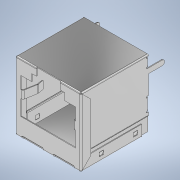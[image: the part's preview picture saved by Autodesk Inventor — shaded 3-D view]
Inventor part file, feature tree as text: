
AUTODESK INVENTOR PART (.ipt)
format: ipt  version: 2020.1 (Build 241239000, 239)  size: 926,208 bytes
history: native  units: mm
features: sheet_metal_op x45, sketch x21, other x20, mirror x7, fillet x1, chamfer x1
ambient origin geometry x8: Origin, YZ Plane, XZ Plane, XY Plane, X Axis, Y Axis, Z Axis, Center Point
bodies: Solid1 (feature_tree)
feature tree (95):
  sheet_metal_op  "Face1"
  sheet_metal_op  "Flange1"
  sheet_metal_op  "Flange2"
  other  "Corner Chamfer1"
  mirror  "Mirror1"
  sheet_metal_op  "Face2"
  mirror  "Mirror2"
  sheet_metal_op  "Fold2"
  mirror  "Mirror3"
  sheet_metal_op  "Fold3"
  sheet_metal_op  "Fold5"
  mirror  "Mirror4"
  sheet_metal_op  "Flange5"
  sketch  "Sketch15"  dims[d11=0.2mm]
  sheet_metal_op  "Face3"
  sheet_metal_op  "Fold7"
  mirror  "Mirror6"
  sheet_metal_op  "Flange8"
  sheet_metal_op  "Flange9"
  sheet_metal_op  "Flange10"
  sheet_metal_op  "Flange11"
  sheet_metal_op  "Flange12"
  sheet_metal_op  "Flange13"
  sheet_metal_op  "Flange14"
  fillet  "Fillet1"  Radius=15.3mm
  mirror  "Mirror7"
  sheet_metal_op  "Flange15"
  sheet_metal_op  "Flange16"
  chamfer  "Corner Round1"
  mirror  "Mirror9"
  sketch  "Sketch1"  dims[d1=16.05mm]
  other  "Plate1"
  sketch  "Sketch3"  dims[d2=0.2mm]
  other  "Plate2"
  sheet_metal_op  "Bend1"
  sheet_metal_op  "Corner1"
  sketch  "Sketch4"  dims[d3=0.435mm]
  other  "Plate3"
  sheet_metal_op  "Bend2"
  sheet_metal_op  "Corner2"
  sketch  "Sketch9"  dims[d4=0.2175mm]
  other  "Plate6"
  sheet_metal_op  "Bend5"
  sketch  "Sketch11"  dims[d5=0.0mm]
  sketch  "Sketch12"  dims[d6=0.1mm]
  sketch  "Sketch13"  dims[d7=16.4mm d8=90.0deg d9=0.1mm]
  sketch  "Sketch14"  dims[d10=0.8mm]
  other  "Plate7"
  sheet_metal_op  "Bend6"
  sheet_metal_op  "Corner5"
  other  "Plate8"
  sheet_metal_op  "Bend7"
  sketch  "Sketch20"  dims[d12=0.1mm]
  sketch  "Sketch21"  dims[d13=0.435mm]
  other  "Plate11"
  sheet_metal_op  "Bend10"
  sheet_metal_op  "Corner8"
  sketch  "Sketch22"  dims[d14=0.2175mm]
  other  "Plate12"
  sheet_metal_op  "Bend11"
  sheet_metal_op  "Corner9"
  sketch  "Sketch23"  dims[d15=0.0mm]
  other  "Plate13"
  sheet_metal_op  "Bend12"
  sheet_metal_op  "Corner10"
  sketch  "Sketch24"  dims[d16=0.1mm]
  other  "Plate14"
  sheet_metal_op  "Bend13"
  sheet_metal_op  "Corner11"
  sketch  "Sketch25"  dims[d17=2.2mm d18=90.0deg d19=0.1mm]
  other  "Plate15"
  sheet_metal_op  "Bend14"
  sheet_metal_op  "Corner12"
  sketch  "Sketch26"  dims[d20=0.8mm]
  other  "Plate16"
  sheet_metal_op  "Bend15"
  sheet_metal_op  "Corner13"
  sketch  "Sketch27"  dims[d21=0.2mm]
  other  "Plate17"
  sheet_metal_op  "Bend16"
  sheet_metal_op  "Corner14"
  sketch  "Sketch28"  dims[d22=0.1mm]
  sketch  "Sketch29"  dims[d23=2.1mm d24=6.0mm d25=45.0deg]
  sketch  "Sketch30"  dims[d51=45.0deg]
  other  "Plate18"
  sheet_metal_op  "Bend17"
  sheet_metal_op  "Corner15"
  sketch  "Sketch31"  dims[d54=16.4mm d55=0.1mm d56=0.435mm d57=0.2175mm d58=0.0mm d59=0.1mm d66=0.2935mm d67=2.101mm d68=0.435mm d69=0.2175mm d70=0.0mm d71=0.1mm d72=90.0deg d73=0.1mm d75=0.435mm d76=0.2175mm d77=0.0mm d78=0.1mm d79=45.0deg d80=0.1mm d89=0.435mm d90=0.2175mm d91=0.0mm d92=0.1mm d93=45.0deg d94=0.1mm d95=0.435mm d96=0.2175mm d97=0.0mm d98=0.1mm d99=14.75mm d100=90.0deg d101=0.1mm d102=0.8mm d103=0.2mm d104=0.1mm d105=135.0deg d106=0.2935mm d107=2.5mm d108=2.101mm d109=0.1mm d110=0.435mm d111=0.2175mm d112=0.0mm d113=0.1mm d179=12.75mm d181=0.118mm d182=0.435mm d183=0.2175mm d184=0.0mm d185=0.1mm d186=90.0deg d187=0.1mm d188=1.0mm d189=1.0mm d190=0.75mm d191=9.3mm d192=20.0mm d194=8.3mm d195=10.0mm d197=10.0mm d199=0.2mm d200=0.0mm d201=0.001mm d202=0.0005mm d203=0.0mm d204=0.1mm d205=0.99mm d206=2.234021mm d207=0.1mm d208=0.8mm d209=0.2mm d210=0.1mm d211=0.001mm d212=0.0005mm d213=0.0mm d214=0.1mm d215=0.99mm d216=2.234021mm d217=0.1mm d218=0.8mm d219=0.2mm d220=0.1mm d221=0.001mm d222=0.0005mm d223=0.0mm d224=0.1mm d225=0.99mm d226=2.234021mm d227=0.1mm d228=0.8mm d229=0.2mm d230=0.1mm d231=0.001mm d232=0.0005mm d233=0.0mm d234=0.1mm d235=0.99mm d236=2.234021mm d237=0.1mm d238=0.8mm d239=0.2mm d240=0.1mm d241=0.435mm d242=0.2175mm d243=0.0mm d244=0.1mm d245=1.68mm d246=0.436mm d247=0.7mm d248=90.0deg d249=0.1mm d250=0.8mm d251=0.2mm d252=0.1mm d253=0.435mm d254=0.2175mm d255=0.0mm d256=0.1mm d257=1.2mm d258=0.0mm d259=3.9mm d260=0.0mm d261=0.1mm d262=0.8mm d263=0.2mm d264=0.1mm d265=0.435mm d266=0.2175mm d267=0.0mm d268=0.1mm d269=2.65mm d270=5.0mm d271=0.7mm d272=90.0deg d273=0.1mm d274=0.8mm d275=0.2mm d276=0.1mm d278=1.7mm d279=1.8mm d280=8.65mm d281=1.8mm d282=1.7mm d283=8.65mm d284=2.975mm d285=1.9mm d286=5.76mm d287=8.04mm d288=13.25mm d289=0.2mm d290=0.2mm d291=0.0mm d292=5.25mm d293=0.3mm d294=0.3mm d295=0.3mm d296=1.2mm d297=1.2mm d298=0.2mm d299=0.0mm d300=0.435mm d301=0.2175mm d302=0.0mm d303=0.1mm d304=3.168mm d305=13.962634mm d306=0.1mm d307=0.8mm d308=0.2mm d309=0.1mm d310=0.435mm d311=0.2175mm d312=0.0mm d313=0.1mm d314=1.516mm d315=3.490659mm d316=0.1mm d317=0.8mm d318=0.2mm d319=0.1mm d320=0.1mm]
  other  "Plate19"
  sheet_metal_op  "Bend18"
  sheet_metal_op  "Corner16"
  other  "Cut4"
  other  "Cut5"
  other  "Cut6"
  other  "Definition1"
